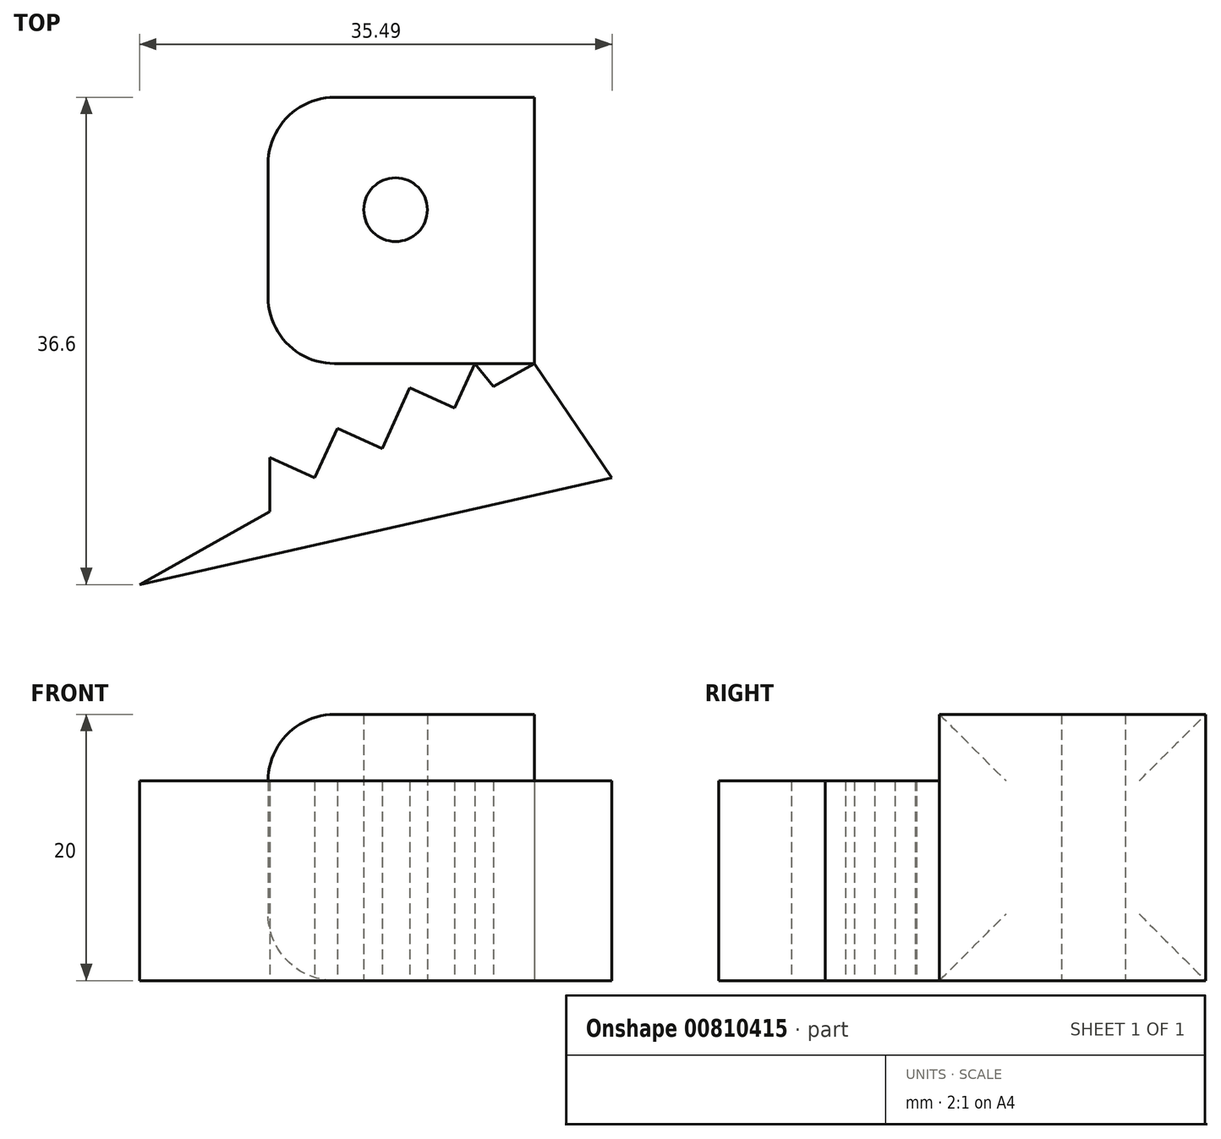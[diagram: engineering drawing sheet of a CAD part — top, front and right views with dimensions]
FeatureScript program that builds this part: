
annotation { "Feature Type Name" : "Feature", "Feature Type Description" : "" }
export const myFeature = defineFeature(function(context is Context, id is Id, definition is map)
    precondition{}
    {
        {
            var Q0;
            Q0=qCreatedBy(makeId("Top.planeOp"),FACE);
            var sketch = newSketch(context, id + "F0", { "sketchPlane" : qUnion([Q0])});
            skLineSegment(sketch, "E0", {"start": v(0, 0) * mm, "end": v(5.84, -8.58) * mm});
            skLineSegment(sketch, "E1", {"start": v(5.84, -8.58) * mm, "end": v(-29.65, -16.6) * mm});
            skLineSegment(sketch, "E2", {"start": v(-29.65, -16.6) * mm, "end": v(0, 0) * mm});
            skSolve(sketch);
        }
        {
            var Q0;
            Q0=makeQuery(id+"F0.imprint","IMPRINT",FACE,{"disambiguationData":[TD([[makeQuery(id+"F0.imprint","IMPRINT",EDGE,{"derivedFrom":sQuery(id+"F0.wireOp",EDGE,"E0")}),-1.0]])]});
            extrude(context, id + "F1", {"entities" : qUnion([Q0]), "depth" : 15 * mm, "offsetDistance" : 25 * mm});
        }
        {
            var Q0;
            Q0=qCreatedBy(makeId("Top.planeOp"),FACE);
            var sketch = newSketch(context, id + "F2", { "sketchPlane" : qUnion([Q0])});
            skLineSegment(sketch, "E3", {"start": v(0, 0) * mm, "end": v(0, 20) * mm});
            skLineSegment(sketch, "E4", {"start": v(0, 20) * mm, "end": v(-20, 20) * mm});
            skLineSegment(sketch, "E5", {"start": v(-20, 20) * mm, "end": v(-20, 0) * mm});
            skLineSegment(sketch, "E6", {"start": v(-20, 0) * mm, "end": v(0, 0) * mm});
            skSolve(sketch);
        }
        {
            var Q0;
            Q0=makeQuery(id+"F2.imprint","IMPRINT",FACE,{"disambiguationData":[TD([[makeQuery(id+"F2.imprint","IMPRINT",EDGE,{"derivedFrom":sQuery(id+"F2.wireOp",EDGE,"E3")}),1.0]])]});
            extrude(context, id + "F3", {"entities" : qUnion([Q0]), "depth" : 20 * mm, "offsetDistance" : 25 * mm});
        }
        {
            var Q0;
            Q0=qCreatedBy(makeId("Top.planeOp"),FACE);
            var sketch = newSketch(context, id + "F4", { "sketchPlane" : qUnion([Q0])});
            skCircle(sketch, "E7", {"center": v(-10.42, 11.56) * mm, "radius": 2.4 * mm});
            skSolve(sketch);
        }
        {
            var Q0;
            Q0=makeQuery(id+"F4.imprint","IMPRINT",FACE,{"disambiguationData":[TD([[makeQuery(id+"F4.imprint","IMPRINT",EDGE,{"derivedFrom":sQuery(id+"F4.wireOp",EDGE,"E7")}),1.0]])]});
            extrude(context, id + "F5", {"entities" : qUnion([Q0]), "operationType" : NewBodyOperationType.REMOVE, "depth" : 25 * mm, "offsetDistance" : 25 * mm});
        }
        {
            var Q0;
            Q0=makeQuery(id+"F1.opExtrude","CAP_FACE",FACE,{"disambiguationData":[OSD([sQuery(id+"F0.wireOp",EDGE,"E0"),sQuery(id+"F0.wireOp",EDGE,"E1"),sQuery(id+"F0.wireOp",EDGE,"E2")])],"isStart":true});
            var sketch = newSketch(context, id + "F6", { "sketchPlane" : qUnion([Q0])});
            skLineSegment(sketch, "E8", {"start": v(0, 0) * mm, "end": v(-4.45, 0) * mm});
            skLineSegment(sketch, "E9", {"start": v(-4.45, 0) * mm, "end": v(-5.98, 3.35) * mm});
            skLineSegment(sketch, "E10", {"start": v(-5.98, 3.35) * mm, "end": v(-9.34, 1.81) * mm});
            skLineSegment(sketch, "E11", {"start": v(-9.34, 1.81) * mm, "end": v(-11.42, 6.4) * mm});
            skLineSegment(sketch, "E12", {"start": v(-11.42, 6.4) * mm, "end": v(-14.8, 4.86) * mm});
            skLineSegment(sketch, "E13", {"start": v(-14.8, 4.86) * mm, "end": v(-16.5, 8.58) * mm});
            skLineSegment(sketch, "E14", {"start": v(-16.5, 8.58) * mm, "end": v(-19.86, 7.05) * mm});
            skLineSegment(sketch, "E15", {"start": v(-19.86, 7.05) * mm, "end": v(-19.86, 14.39) * mm});
            skLineSegment(sketch, "E16", {"start": v(-19.86, 14.39) * mm, "end": v(2.92, 9.24) * mm});
            skPoint(sketch, "E16.endSnap0", {"position": v(2.92, 4.3) * mm});
            skLineSegment(sketch, "E17", {"start": v(2.92, 9.24) * mm, "end": v(-4.45, 0) * mm});
            skSolve(sketch);
        }
        {
            var Q0;
            {var subQ0=sQuery(id+"F6.wireOp",EDGE,"E9");Q0=makeQuery(id+"F6.imprint","IMPRINT",FACE,{"disambiguationData":[TD([[makeQuery(id+"F6.imprint","IMPRINT",EDGE,{"derivedFrom":subQ0}),-1.0]])]});}
            var Q1;
            {var subQ0=sQuery(id+"F6.wireOp",EDGE,"E10");Q1=makeQuery(id+"F6.imprint","IMPRINT",FACE,{"disambiguationData":[TD([[makeQuery(id+"F6.imprint","IMPRINT",EDGE,{"derivedFrom":subQ0}),-1.0]])]});}
            var Q2;
            {var subQ4=sQuery(id+"F6.wireOp",EDGE,"E12");Q2=makeQuery(id+"F6.imprint","IMPRINT",FACE,{"disambiguationData":[TD([[makeQuery(id+"F6.imprint","IMPRINT",EDGE,{"derivedFrom":subQ4}),-1.0]])]});}
            extrude(context, id + "F7", {"entities" : qUnion([Q0, Q1, Q2]), "operationType" : NewBodyOperationType.ADD, "oppositeDirection" : true, "depth" : 15 * mm, "offsetDistance" : 25 * mm});
        }
        {
            var Q0;
            Q0=makeQuery(id+"F3.opExtrude","SWEPT_FACE",FACE,{"disambiguationData":[OSD([sQuery(id+"F2.wireOp",EDGE,"E5")])]});
            fillet(context, id + "F8", {"entities" : qUnion([Q0]), "radius" : 5 * mm, "tangentPropagation" : true, "allowEdgeOverflow" : false});
        }
    });
